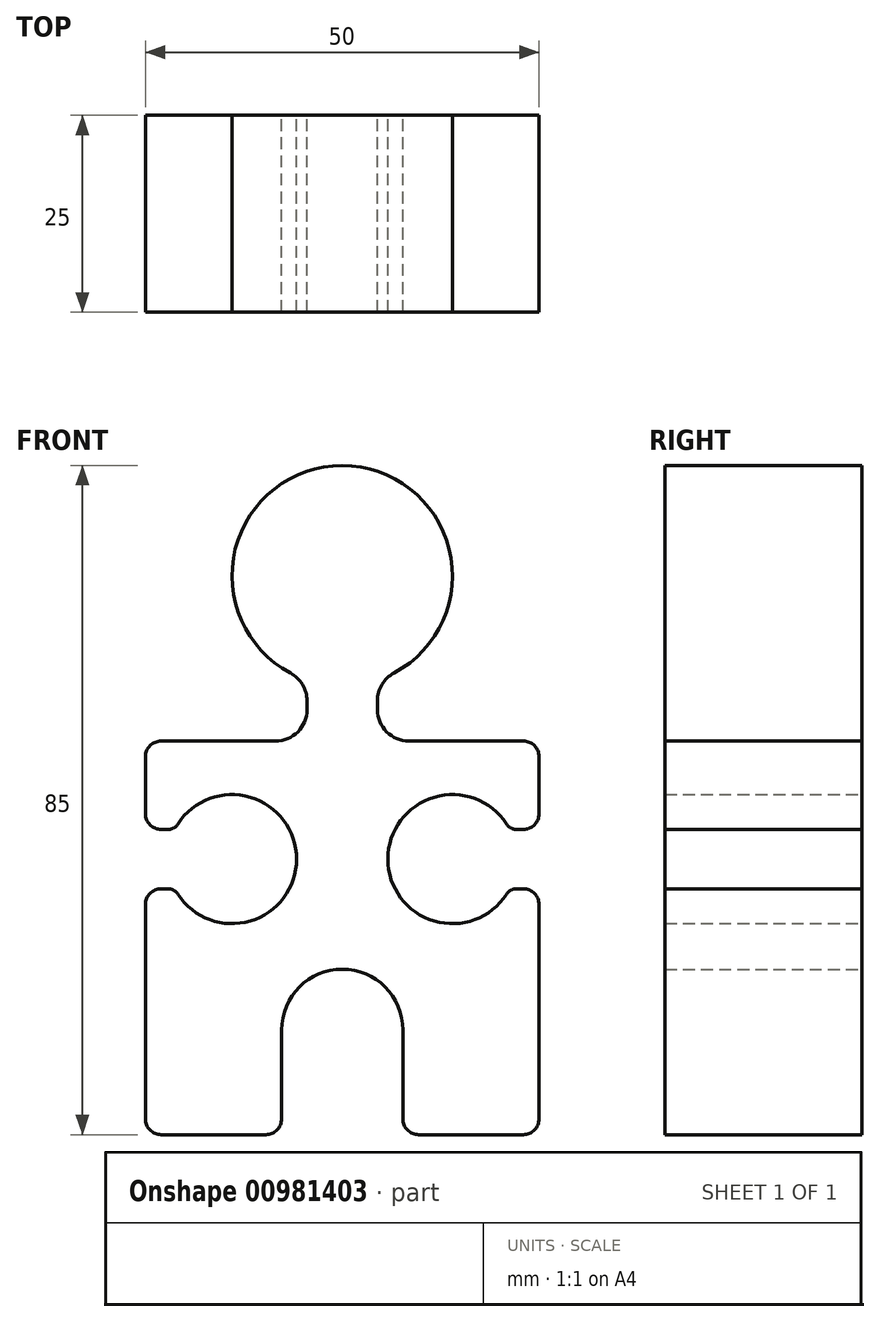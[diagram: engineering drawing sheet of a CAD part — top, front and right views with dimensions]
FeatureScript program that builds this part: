
annotation { "Feature Type Name" : "Feature", "Feature Type Description" : "" }
export const myFeature = defineFeature(function(context is Context, id is Id, definition is map)
    precondition{}
    {
        {
            var Q0;
            Q0=qCreatedBy(makeId("Front.planeOp"),FACE);
            var sketch = newSketch(context, id + "F0", { "sketchPlane" : qUnion([Q0])});
            skLineSegment(sketch, "E0.bottom", {"start": v(-41.23, -23.79) * mm, "end": v(-27.93, -23.79) * mm});
            skLineSegment(sketch, "E0.top", {"start": v(-41.23, 26.21) * mm, "end": v(-26.7, 26.21) * mm});
            skLineSegment(sketch, "E0.left", {"start": v(-43.23, -21.79) * mm, "end": v(-43.23, 5.44) * mm});
            skLineSegment(sketch, "E0.right", {"start": v(6.77, -21.79) * mm, "end": v(6.77, 5.44) * mm});
            skPoint(sketch, "E0.middle", {"position": v(-18.23, 1.21) * mm});
            skLineSegment(sketch, "E1.trimOffspring", {"start": v(-43.23, 16.99) * mm, "end": v(-43.23, 24.21) * mm});
            skPoint(sketch, "E2.visualSharp", {"position": v(-43.23, 14.49) * mm});
            skPoint(sketch, "E3.visualSharp", {"position": v(-43.23, 7.94) * mm});
            skPoint(sketch, "E4.MirrorP", {"position": v(6.77, 7.71) * mm});
            skLineSegment(sketch, "E5.trimOffspring", {"start": v(6.77, 16.99) * mm, "end": v(6.77, 24.21) * mm});
            skArc(sketch, "E6", {"start": v(-10.53, -10.49) * mm, "mid": v(-18.23, -2.79) * mm, "end": v(-25.93, -10.49) * mm});
            skLineSegment(sketch, "E7", {"start": v(-25.93, -10.49) * mm, "end": v(-25.93, -21.79) * mm});
            skLineSegment(sketch, "E8.MirrorCS", {"start": v(-10.53, -10.49) * mm, "end": v(-10.53, -21.79) * mm});
            skLineSegment(sketch, "E9.trimOffspring", {"start": v(-8.53, -23.79) * mm, "end": v(4.77, -23.79) * mm});
            skArc(sketch, "E10", {"start": v(-11.64, 34.86) * mm, "mid": v(-18.23, 61.21) * mm, "end": v(-24.81, 34.86) * mm});
            skPoint(sketch, "E11.endSnap0", {"position": v(-18.23, 26.21) * mm});
            skLineSegment(sketch, "E12.0", {"start": v(-22.7, 31.33) * mm, "end": v(-22.7, 30.21) * mm});
            skLineSegment(sketch, "E13.0", {"start": v(-13.76, 31.33) * mm, "end": v(-13.76, 30.21) * mm});
            skPoint(sketch, "E14.orphan", {"position": v(-18.23, 21.46) * mm});
            skLineSegment(sketch, "E15.trimOffspring", {"start": v(-9.76, 26.21) * mm, "end": v(4.77, 26.21) * mm});
            skPoint(sketch, "E11.start.orphan", {"position": v(-18.23, 38.37) * mm});
            skPoint(sketch, "E16.visualSharp", {"position": v(-22.7, 26.21) * mm});
            skArc(sketch, "E16.filletArc", {"start": v(-26.7, 26.21) * mm, "mid": v(-23.87, 27.39) * mm, "end": v(-22.7, 30.21) * mm});
            skPoint(sketch, "E17.visualSharp", {"position": v(-13.76, 26.21) * mm});
            skArc(sketch, "E17.filletArc", {"start": v(-13.76, 30.21) * mm, "mid": v(-12.58, 27.39) * mm, "end": v(-9.76, 26.21) * mm});
            skPoint(sketch, "E18.visualSharp", {"position": v(-13.76, 33.95) * mm});
            skArc(sketch, "E18.filletArc", {"start": v(-11.64, 34.86) * mm, "mid": v(-13.19, 33.4) * mm, "end": v(-13.76, 31.33) * mm});
            skPoint(sketch, "E19.visualSharp", {"position": v(-22.7, 33.95) * mm});
            skArc(sketch, "E19.filletArc", {"start": v(-22.7, 31.33) * mm, "mid": v(-23.27, 33.4) * mm, "end": v(-24.81, 34.86) * mm});
            skPoint(sketch, "E20.visualSharp", {"position": v(-43.23, 26.21) * mm});
            skArc(sketch, "E20.filletArc", {"start": v(-41.23, 26.21) * mm, "mid": v(-42.64, 25.63) * mm, "end": v(-43.23, 24.21) * mm});
            skPoint(sketch, "E21.visualSharp", {"position": v(6.77, 26.21) * mm});
            skArc(sketch, "E21.filletArc", {"start": v(6.77, 24.21) * mm, "mid": v(6.19, 25.63) * mm, "end": v(4.77, 26.21) * mm});
            skPoint(sketch, "E22.visualSharp", {"position": v(6.77, -23.79) * mm});
            skArc(sketch, "E22.filletArc", {"start": v(4.77, -23.79) * mm, "mid": v(6.19, -23.2) * mm, "end": v(6.77, -21.79) * mm});
            skPoint(sketch, "E23.visualSharp", {"position": v(-10.53, -23.79) * mm});
            skArc(sketch, "E23.filletArc", {"start": v(-10.53, -21.79) * mm, "mid": v(-9.94, -23.2) * mm, "end": v(-8.53, -23.79) * mm});
            skPoint(sketch, "E24.visualSharp", {"position": v(-25.93, -23.79) * mm});
            skArc(sketch, "E24.filletArc", {"start": v(-27.93, -23.79) * mm, "mid": v(-26.51, -23.2) * mm, "end": v(-25.93, -21.79) * mm});
            skPoint(sketch, "E25.visualSharp", {"position": v(-43.23, -23.79) * mm});
            skArc(sketch, "E25.filletArc", {"start": v(-43.23, -21.79) * mm, "mid": v(-42.64, -23.2) * mm, "end": v(-41.23, -23.79) * mm});
            skArc(sketch, "E26.MirrorCS", {"start": v(-41.23, 14.99) * mm, "mid": v(-42.64, 15.57) * mm, "end": v(-43.23, 16.99) * mm});
            skArc(sketch, "E27.MirrorCS", {"start": v(-43.23, 5.44) * mm, "mid": v(-42.64, 6.86) * mm, "end": v(-41.23, 7.44) * mm});
            skPoint(sketch, "E28.MirrorP", {"position": v(-39.2, 7.94) * mm});
            skLineSegment(sketch, "E29.1", {"start": v(-40.37, 14.99) * mm, "end": v(-41.23, 14.99) * mm});
            skArc(sketch, "E29.2", {"start": v(-39.1, 15.67) * mm, "mid": v(-39.65, 15.17) * mm, "end": v(-40.37, 14.99) * mm});
            skLineSegment(sketch, "E29.4", {"start": v(-40.37, 7.44) * mm, "end": v(-41.23, 7.44) * mm});
            skArc(sketch, "E29.5", {"start": v(-40.37, 7.44) * mm, "mid": v(-39.65, 7.26) * mm, "end": v(-39.1, 6.76) * mm});
            skArc(sketch, "E29.6", {"start": v(-39.1, 15.67) * mm, "mid": v(-24.03, 11.21) * mm, "end": v(-39.1, 6.76) * mm});
            skLineSegment(sketch, "E30", {"start": v(-18.23, 21.46) * mm, "end": v(-18.23, 1.21) * mm});
            skArc(sketch, "E31.MirrorCS", {"start": v(2.66, 15.67) * mm, "mid": v(-12.43, 11.21) * mm, "end": v(2.66, 6.76) * mm});
            skArc(sketch, "E32.MirrorCS", {"start": v(4.77, 14.99) * mm, "mid": v(6.19, 15.57) * mm, "end": v(6.77, 16.99) * mm});
            skLineSegment(sketch, "E33.MirrorCS", {"start": v(3.92, 14.99) * mm, "end": v(4.77, 14.99) * mm});
            skArc(sketch, "E34.MirrorCS", {"start": v(2.66, 15.67) * mm, "mid": v(3.2, 15.17) * mm, "end": v(3.92, 14.99) * mm});
            skArc(sketch, "E35.MirrorCS", {"start": v(3.92, 7.44) * mm, "mid": v(3.2, 7.26) * mm, "end": v(2.66, 6.76) * mm});
            skLineSegment(sketch, "E36.MirrorCS", {"start": v(3.92, 7.44) * mm, "end": v(4.77, 7.44) * mm});
            skArc(sketch, "E37.MirrorCS", {"start": v(6.77, 5.44) * mm, "mid": v(6.19, 6.86) * mm, "end": v(4.77, 7.44) * mm});
            skSolve(sketch);
        }
        {
            var Q0;
            Q0=makeQuery(id+"F0.imprint","IMPRINT",FACE,{"disambiguationData":[TD([[makeQuery(id+"F0.imprint","IMPRINT",EDGE,{"derivedFrom":sQuery(id+"F0.wireOp",EDGE,"E0.bottom")}),1.0]])]});
            extrude(context, id + "F1", {"entities" : qUnion([Q0]), "depth" : 25 * mm, "offsetDistance" : 25 * mm});
        }
    });
